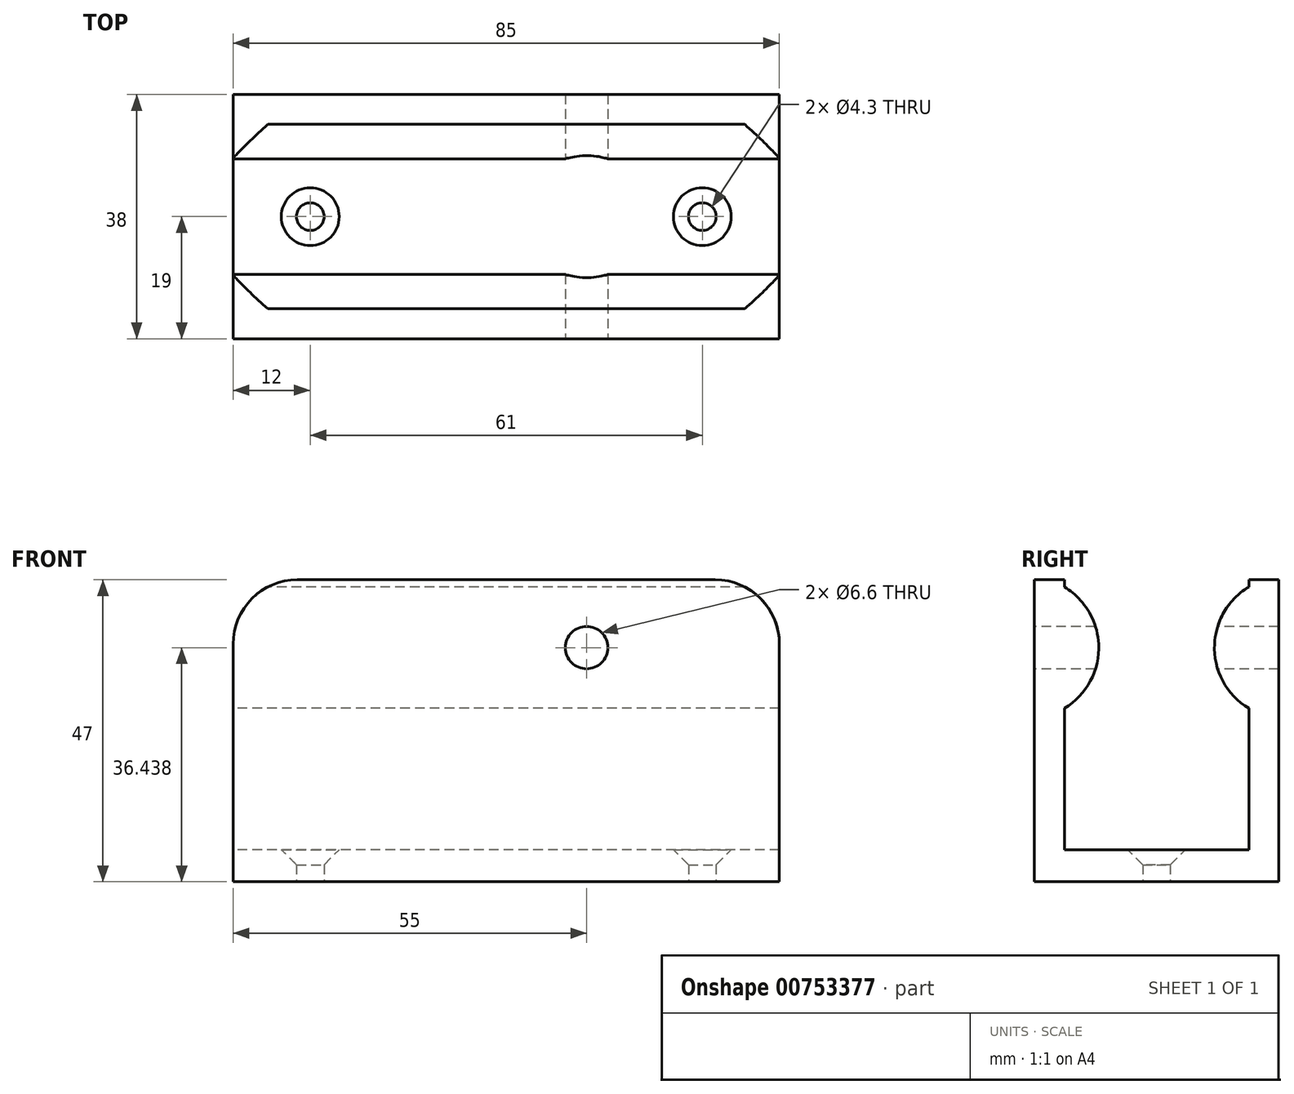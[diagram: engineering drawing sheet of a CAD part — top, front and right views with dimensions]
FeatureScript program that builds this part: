
annotation { "Feature Type Name" : "Feature", "Feature Type Description" : "" }
export const myFeature = defineFeature(function(context is Context, id is Id, definition is map)
    precondition{}
    {
        {
            var Q0;
            Q0=qCreatedBy(makeId("Front.planeOp"),FACE);
            var sketch = newSketch(context, id + "F0", { "sketchPlane" : qUnion([Q0])});
            skLineSegment(sketch, "E0.bottom", {"start": v(-42.5, 23.5) * mm, "end": v(42.5, 23.5) * mm});
            skLineSegment(sketch, "E0.top", {"start": v(-42.5, -23.5) * mm, "end": v(42.5, -23.5) * mm});
            skLineSegment(sketch, "E0.left", {"start": v(-42.5, 23.5) * mm, "end": v(-42.5, -23.5) * mm});
            skLineSegment(sketch, "E0.right", {"start": v(42.5, 23.5) * mm, "end": v(42.5, -23.5) * mm});
            skLineSegment(sketch, "E1", {"start": v(-42.5, 23.5) * mm, "end": v(42.5, -23.5) * mm, "construction": true});
            skSolve(sketch);
        }
        {
            var Q0;
            Q0=qSketchRegion(id+"F0",true);
            extrude(context, id + "F1", {"entities" : qUnion([Q0]), "depth" : 38 * mm, "symmetric" : true});
        }
        {
            var Q0;
            Q0=makeQuery(id+"F1.opExtrude","SWEPT_FACE",FACE,{"disambiguationData":[OSD([sQuery(id+"F0.wireOp",EDGE,"E0.left")])]});
            var sketch = newSketch(context, id + "F2", { "sketchPlane" : qUnion([Q0])});
            skLineSegment(sketch, "E2", {"start": v(0, 0) * mm, "end": v(0, 25.7) * mm, "construction": true});
            skPoint(sketch, "E2.endSnap0", {"position": v(0, 23.5) * mm});
            skLineSegment(sketch, "E3", {"start": v(-14.35, -18.5) * mm, "end": v(14.35, -18.5) * mm});
            skLineSegment(sketch, "E4", {"start": v(14.35, -18.5) * mm, "end": v(14.35, 3.5) * mm});
            skLineSegment(sketch, "E5", {"start": v(-14.35, -18.5) * mm, "end": v(-14.35, 3.5) * mm});
            skLineSegment(sketch, "E6", {"start": v(-14.35, 22.38) * mm, "end": v(-14.35, 23.5) * mm});
            skLineSegment(sketch, "E7", {"start": v(-14.35, 23.5) * mm, "end": v(14.35, 23.5) * mm});
            skLineSegment(sketch, "E8", {"start": v(14.35, 23.5) * mm, "end": v(14.35, 22.38) * mm});
            skArc(sketch, "E9", {"start": v(-14.35, 3.5) * mm, "mid": v(-9, 12.94) * mm, "end": v(-14.35, 22.38) * mm});
            skArc(sketch, "E10", {"start": v(14.35, 22.38) * mm, "mid": v(9, 12.94) * mm, "end": v(14.35, 3.5) * mm});
            skSolve(sketch);
        }
        {
            var Q0;
            Q0=qSketchRegion(id+"F2",true);
            extrude(context, id + "F3", {"entities" : qUnion([Q0]), "operationType" : NewBodyOperationType.REMOVE, "endBound" : BoundingType.THROUGH_ALL, "oppositeDirection" : true, "depth" : 25 * mm});
        }
        {
            var Q0;
            Q0=makeQuery(id+"F1.opExtrude","CAP_FACE",FACE,{"disambiguationData":[OSD([sQuery(id+"F0.wireOp",EDGE,"E0.bottom"),sQuery(id+"F0.wireOp",EDGE,"E0.top"),sQuery(id+"F0.wireOp",EDGE,"E0.left"),sQuery(id+"F0.wireOp",EDGE,"E0.right")])],"isStart":false});
            var sketch = newSketch(context, id + "F4", { "sketchPlane" : qUnion([Q0])});
            skCircle(sketch, "E11", {"center": v(12.5, 12.94) * mm, "radius": 3.3 * mm});
            skLineSegment(sketch, "E12", {"start": v(-42.5, 12.94) * mm, "end": v(12.5, 12.94) * mm, "construction": true});
            skSolve(sketch);
        }
        {
            var Q0;
            Q0=qSketchRegion(id+"F4",true);
            extrude(context, id + "F5", {"entities" : qUnion([Q0]), "operationType" : NewBodyOperationType.REMOVE, "endBound" : BoundingType.THROUGH_ALL, "oppositeDirection" : true, "depth" : 25 * mm});
        }
        {
            var Q0;
            Q0=makeQuery(id+"F3.boolean.opBoolean","COPY",FACE,{"derivedFrom":makeQuery(id+"F3.opExtrude","SWEPT_FACE",FACE,{"disambiguationData":[OSD([sQuery(id+"F2.wireOp",EDGE,"E3")])]})});
            var sketch = newSketch(context, id + "F6", { "sketchPlane" : qUnion([Q0])});
            skPoint(sketch, "E13", {"position": v(-30.5, 0) * mm});
            skPoint(sketch, "E14", {"position": v(30.5, 0) * mm});
            skLineSegment(sketch, "E15", {"start": v(-30.5, 0) * mm, "end": v(30.5, 0) * mm, "construction": true});
            skSolve(sketch);
        }
        {
            var Q0;
            Q0=sQuery(id+"F6.wireOp",VERTEX,"E13");
            var Q1;
            Q1=sQuery(id+"F6.wireOp",VERTEX,"E14");
            var Q2;
            Q2=makeQuery(id+"F1.opExtrude","SWEPT_BODY",BODY,{"disambiguationData":[OSD([sQuery(id+"F0.wireOp",EDGE,"E0.bottom"),sQuery(id+"F0.wireOp",EDGE,"E0.top"),sQuery(id+"F0.wireOp",EDGE,"E0.left"),sQuery(id+"F0.wireOp",EDGE,"E0.right")])]});
            hole(context, id + "F7", {"style" : HoleStyle.C_SINK, "endStyle" : HoleEndStyle.THROUGH, "holeDiameter" : 4.3 * mm, "cSinkDiameter" : 9 * mm, "cSinkAngle" : 90 * degree, "isTappedThrough" : true, "tappedDepth" : 12 * mm, "tapClearance" : 3, "locations" : qUnion([Q0, Q1]), "scope" : qUnion([Q2])});
        }
        {
            var Q0;
            {var subQ0=sQuery(id+"F0.wireOp",EDGE,"E0.bottom");var subQ1=sQuery(id+"F0.wireOp",EDGE,"E0.left");Q0=makeQuery(id+"F3.boolean.opBoolean","SPLIT",EDGE,{"disambiguationData":[TD([makeQuery(id+"F3.opExtrude","SWEPT_FACE",FACE,{"disambiguationData":[OSD([sQuery(id+"F2.wireOp",EDGE,"E6")])]})])],"derivedFrom":makeQuery(id+"F1.opExtrude","SWEPT_EDGE",EDGE,{"disambiguationData":[OSD([subQ0,subQ1])]})});}
            var Q1;
            {var subQ0=sQuery(id+"F0.wireOp",EDGE,"E0.bottom");var subQ1=sQuery(id+"F0.wireOp",EDGE,"E0.left");Q1=makeQuery(id+"F3.boolean.opBoolean","SPLIT",EDGE,{"disambiguationData":[TD([makeQuery(id+"F3.opExtrude","SWEPT_FACE",FACE,{"disambiguationData":[OSD([sQuery(id+"F2.wireOp",EDGE,"E8")])]})])],"derivedFrom":makeQuery(id+"F1.opExtrude","SWEPT_EDGE",EDGE,{"disambiguationData":[OSD([subQ0,subQ1])]})});}
            var Q2;
            {var subQ0=sQuery(id+"F0.wireOp",EDGE,"E0.bottom");var subQ1=sQuery(id+"F0.wireOp",EDGE,"E0.right");Q2=makeQuery(id+"F3.boolean.opBoolean","SPLIT",EDGE,{"disambiguationData":[TD([makeQuery(id+"F3.opExtrude","SWEPT_FACE",FACE,{"disambiguationData":[OSD([sQuery(id+"F2.wireOp",EDGE,"E6")])]})])],"derivedFrom":makeQuery(id+"F1.opExtrude","SWEPT_EDGE",EDGE,{"disambiguationData":[OSD([subQ0,subQ1])]})});}
            var Q3;
            {var subQ0=sQuery(id+"F0.wireOp",EDGE,"E0.bottom");var subQ1=sQuery(id+"F0.wireOp",EDGE,"E0.right");Q3=makeQuery(id+"F3.boolean.opBoolean","SPLIT",EDGE,{"disambiguationData":[TD([makeQuery(id+"F3.opExtrude","SWEPT_FACE",FACE,{"disambiguationData":[OSD([sQuery(id+"F2.wireOp",EDGE,"E8")])]})])],"derivedFrom":makeQuery(id+"F1.opExtrude","SWEPT_EDGE",EDGE,{"disambiguationData":[OSD([subQ0,subQ1])]})});}
            fillet(context, id + "F8", {"entities" : qUnion([Q0, Q1, Q2, Q3]), "radius" : 10 * mm, "tangentPropagation" : true, "allowEdgeOverflow" : false});
        }
    });
